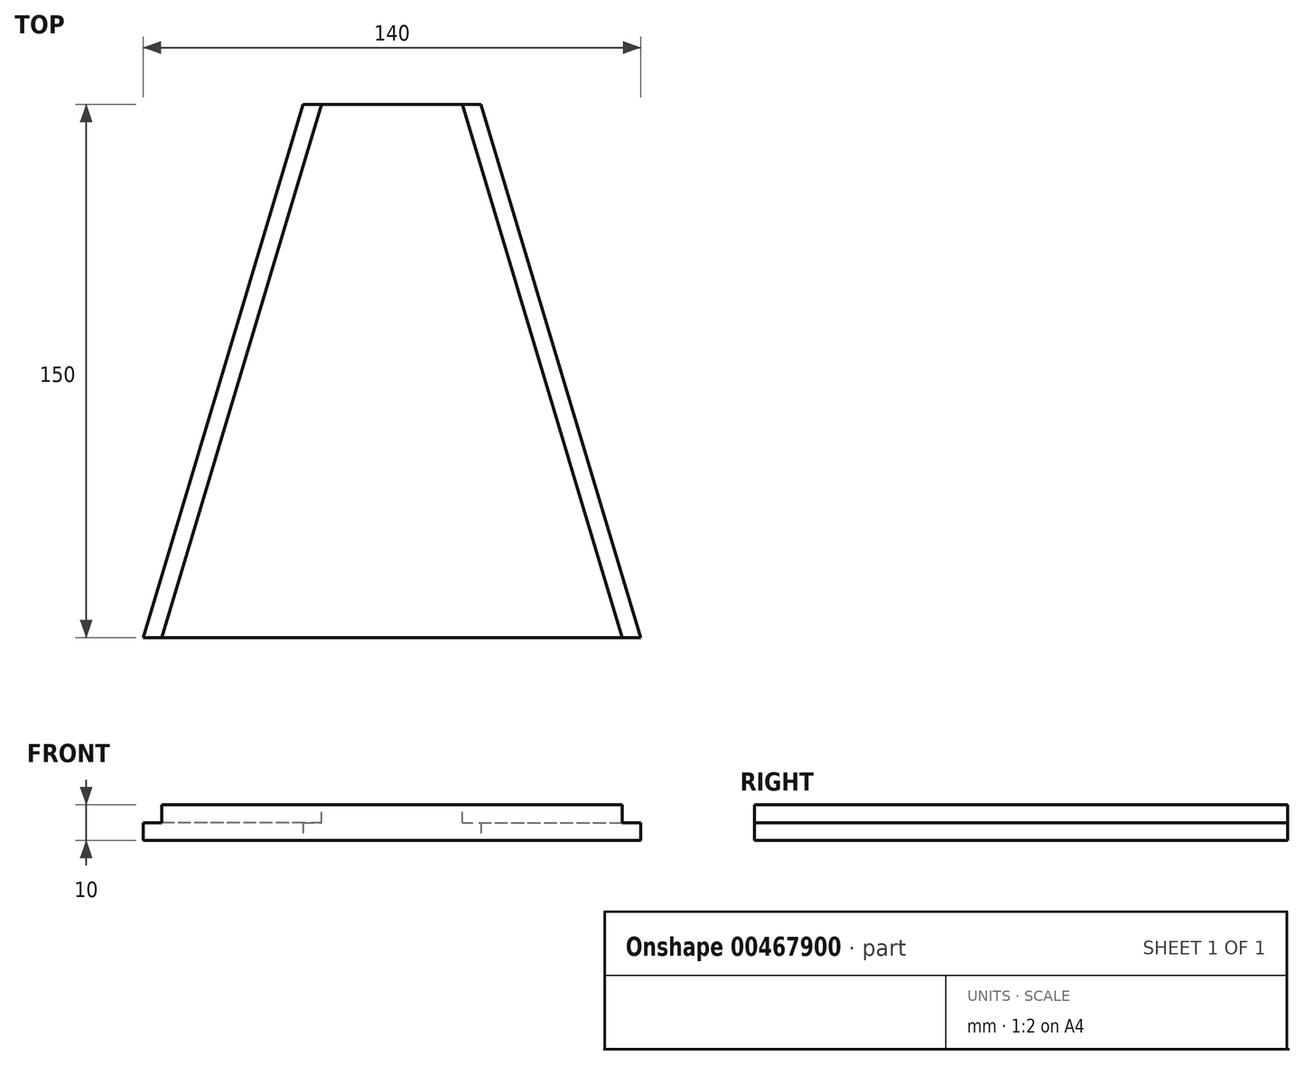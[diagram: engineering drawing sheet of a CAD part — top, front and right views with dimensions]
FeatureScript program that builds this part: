
annotation { "Feature Type Name" : "Feature", "Feature Type Description" : "" }
export const myFeature = defineFeature(function(context is Context, id is Id, definition is map)
    precondition{}
    {
        {
            var Q0;
            Q0=qCreatedBy(makeId("Top.planeOp"),FACE);
            var sketch = newSketch(context, id + "F0", { "sketchPlane" : qUnion([Q0])});
            skLineSegment(sketch, "E0.bottom", {"start": v(-5.02, 74.92) * mm, "end": v(44.98, 74.92) * mm});
            skLineSegment(sketch, "E0.top", {"start": v(-50.02, -75.08) * mm, "end": v(89.98, -75.08) * mm});
            skLineSegment(sketch, "E1.top", {"start": v(-5.02, -75.08) * mm, "end": v(44.98, -75.08) * mm});
            skLineSegment(sketch, "E2", {"start": v(-5.02, 74.92) * mm, "end": v(-50.02, -75.08) * mm});
            skLineSegment(sketch, "E3", {"start": v(44.98, 74.92) * mm, "end": v(89.98, -75.08) * mm});
            skSolve(sketch);
        }
        {
            var Q0;
            Q0 = qSketchRegion(id + "F0", true);
            extrude(context, id + "F1", {"entities" : qUnion([Q0]), "depth" : 10 * mm});
        }
        {
            var Q0;
            Q0=makeQuery(id+"F1.opExtrude","CAP_FACE",FACE,{"disambiguationData":[OSD([sQuery(id+"F0.wireOp",EDGE,"E0.top"),sQuery(id+"F0.wireOp",EDGE,"E0.bottom"),sQuery(id+"F0.wireOp",EDGE,"E1.top"),sQuery(id+"F0.wireOp",EDGE,"E2"),sQuery(id+"F0.wireOp",EDGE,"E3")])],"isStart":false});
            var sketch = newSketch(context, id + "F2", { "sketchPlane" : qUnion([Q0])});
            skLineSegment(sketch, "E4", {"start": v(39.76, 74.92) * mm, "end": v(84.76, -75.08) * mm});
            skLineSegment(sketch, "E5", {"start": v(39.76, 74.92) * mm, "end": v(44.98, 74.92) * mm});
            skLineSegment(sketch, "E6", {"start": v(44.98, 74.92) * mm, "end": v(89.98, -75.08) * mm});
            skLineSegment(sketch, "E7", {"start": v(89.98, -75.08) * mm, "end": v(84.76, -75.08) * mm});
            skLineSegment(sketch, "E8", {"start": v(0.2, 74.92) * mm, "end": v(-44.8, -75.08) * mm});
            skLineSegment(sketch, "E9", {"start": v(0.2, 74.92) * mm, "end": v(-5.02, 74.92) * mm});
            skLineSegment(sketch, "E10", {"start": v(-5.02, 74.92) * mm, "end": v(-50.02, -75.08) * mm});
            skLineSegment(sketch, "E11", {"start": v(-50.02, -75.08) * mm, "end": v(-44.8, -75.08) * mm});
            skSolve(sketch);
        }
        {
            var Q0;
            Q0 = qSketchRegion(id + "F2", true);
            extrude(context, id + "F3", {"entities" : qUnion([Q0]), "operationType" : NewBodyOperationType.REMOVE, "oppositeDirection" : true, "depth" : 5 * mm});
        }
        {
            var Q0;
            Q0 = qSketchRegion(id + "F2", true);
            extrude(context, id + "F4", {"entities" : qUnion([Q0]), "operationType" : NewBodyOperationType.REMOVE, "oppositeDirection" : true, "depth" : 5 * mm});
        }
    });
